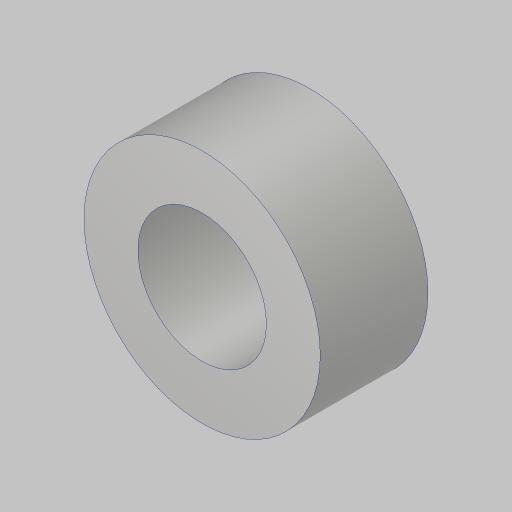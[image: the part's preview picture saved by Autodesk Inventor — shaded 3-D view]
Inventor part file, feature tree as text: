
AUTODESK INVENTOR PART (.ipt)
format: ipt  version: 2023.5 (Build 275446000, 446)  size: 105,984 bytes
history: native  units: in
note: dims shown in document units (in); Inventor stores cm internally (conversion verified against a paired STEP export)
features: extrude x1, sketch x1
ambient origin geometry x8: Origin, YZ Plane, XZ Plane, XY Plane, X Axis, Y Axis, Z Axis, Center Point
bodies: Solid1 (feature_tree)
feature tree (2):
  extrude  "Extrusion1"  Depth=0.75in
  sketch  "Sketch1"  dims[d0=0.375in d1=0.895in d2=0.75in d3=0.0in]
